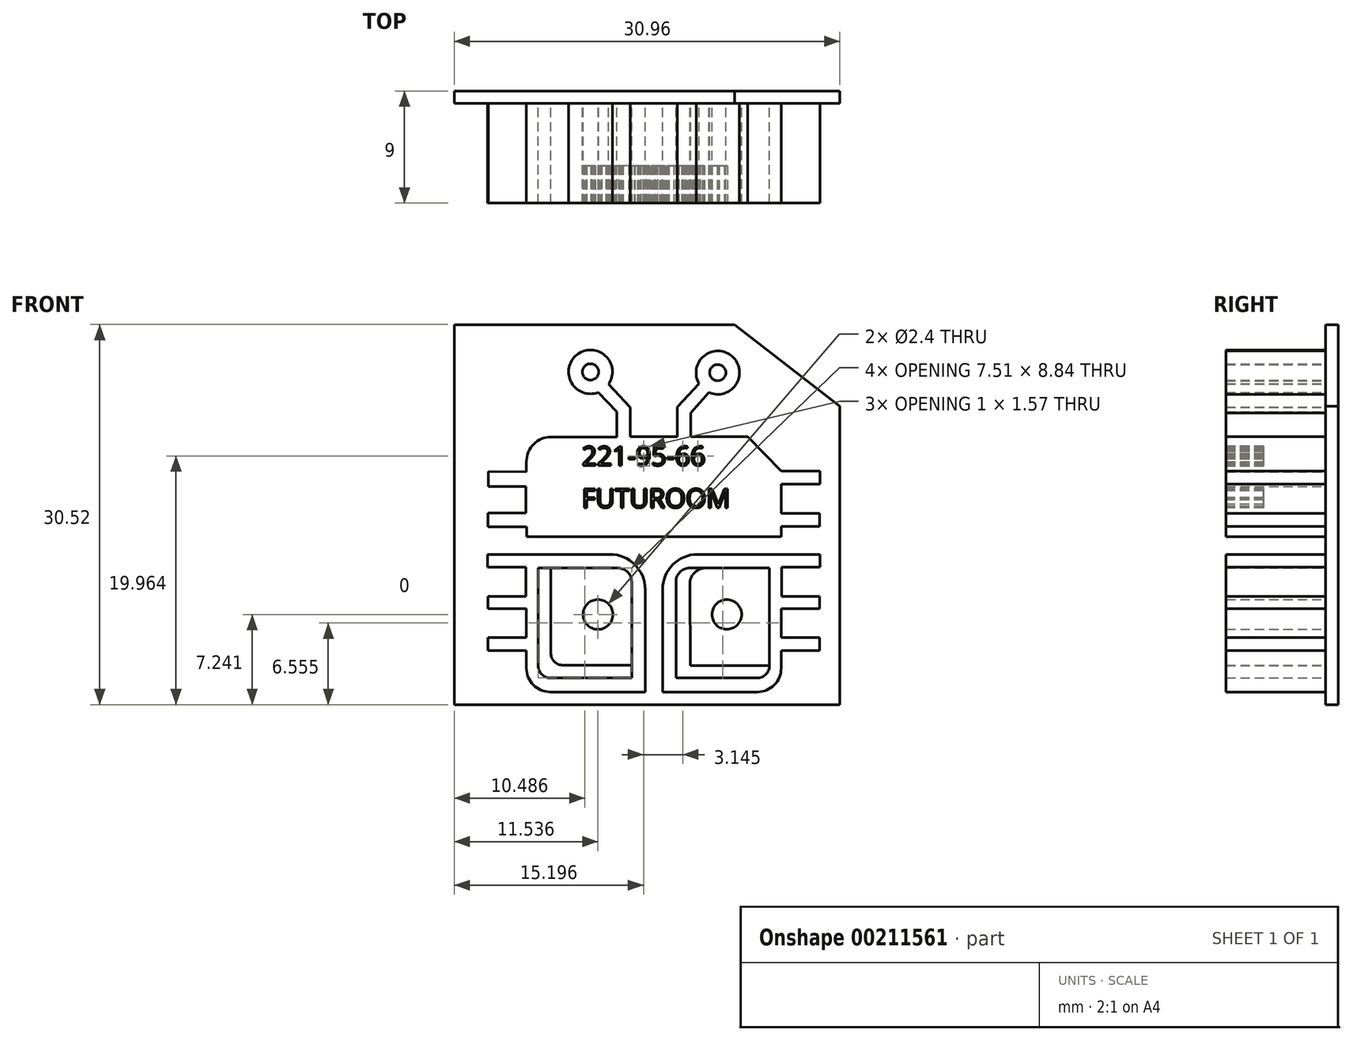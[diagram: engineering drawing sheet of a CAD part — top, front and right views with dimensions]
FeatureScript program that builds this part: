
annotation { "Feature Type Name" : "Feature", "Feature Type Description" : "" }
export const myFeature = defineFeature(function(context is Context, id is Id, definition is map)
    precondition{}
    {
        {
            var Q0;
            Q0=qCreatedBy(makeId("Front.planeOp"),FACE);
            var sketch = newSketch(context, id + "F0", { "sketchPlane" : qUnion([Q0])});
            skLineSegment(sketch, "E0", {"start": v(-14.86, -3.78) * mm, "end": v(-14.86, -5) * mm});
            skLineSegment(sketch, "E1", {"start": v(-14.86, -5) * mm, "end": v(-11.84, -5) * mm});
            skLineSegment(sketch, "E2", {"start": v(-11.84, -5) * mm, "end": v(-11.84, -7.14) * mm});
            skLineSegment(sketch, "E3", {"start": v(-11.84, -7.14) * mm, "end": v(-14.87, -7.14) * mm});
            skLineSegment(sketch, "E4", {"start": v(-14.87, -7.14) * mm, "end": v(-14.87, -8.25) * mm});
            skLineSegment(sketch, "E5", {"start": v(-14.87, -8.25) * mm, "end": v(-11.76, -8.25) * mm});
            skLineSegment(sketch, "E6", {"start": v(-11.76, -8.25) * mm, "end": v(-11.76, -9.03) * mm});
            skLineSegment(sketch, "E7", {"start": v(-11.76, -9.03) * mm, "end": v(8.67, -9.03) * mm});
            skLineSegment(sketch, "E8", {"start": v(8.67, -9.03) * mm, "end": v(8.67, -8.21) * mm});
            skLineSegment(sketch, "E9", {"start": v(8.67, -8.21) * mm, "end": v(11.76, -8.21) * mm});
            skLineSegment(sketch, "E10", {"start": v(11.76, -8.21) * mm, "end": v(11.76, -7.17) * mm});
            skLineSegment(sketch, "E11", {"start": v(11.76, -7.17) * mm, "end": v(8.68, -7.17) * mm});
            skLineSegment(sketch, "E12", {"start": v(8.68, -7.17) * mm, "end": v(8.68, -4.82) * mm});
            skLineSegment(sketch, "E13", {"start": v(8.68, -4.82) * mm, "end": v(11.8, -4.82) * mm});
            skLineSegment(sketch, "E14", {"start": v(11.8, -4.82) * mm, "end": v(11.8, -3.78) * mm});
            skLineSegment(sketch, "E15", {"start": v(11.8, -3.78) * mm, "end": v(8.68, -3.78) * mm});
            skLineSegment(sketch, "E16", {"start": v(8.68, -3.78) * mm, "end": v(5.96, -1) * mm});
            skLineSegment(sketch, "E17", {"start": v(5.96, -1) * mm, "end": v(1.42, -1) * mm});
            skLineSegment(sketch, "E18", {"start": v(1.42, -1) * mm, "end": v(1.42, 0.89) * mm});
            skLineSegment(sketch, "E19", {"start": v(1.42, 0.89) * mm, "end": v(2.86, 2.55) * mm});
            skLineSegment(sketch, "E20", {"start": v(2.08, 3.25) * mm, "end": v(0.33, 1.37) * mm});
            skLineSegment(sketch, "E21", {"start": v(0.33, 1.37) * mm, "end": v(0.33, -1) * mm});
            skLineSegment(sketch, "E22", {"start": v(0.33, -1) * mm, "end": v(-3.46, -1) * mm});
            skLineSegment(sketch, "E23", {"start": v(-3.46, -1) * mm, "end": v(-3.46, 1.34) * mm});
            skLineSegment(sketch, "E24", {"start": v(-3.46, 1.34) * mm, "end": v(-5.19, 3.2) * mm});
            skLineSegment(sketch, "E25", {"start": v(-6.02, 2.55) * mm, "end": v(-4.54, 1) * mm});
            skLineSegment(sketch, "E26", {"start": v(-4.54, 1) * mm, "end": v(-4.54, -1.02) * mm});
            skLineSegment(sketch, "E27", {"start": v(-4.54, -1.02) * mm, "end": v(-9.8, -1.02) * mm});
            skLineSegment(sketch, "E28", {"start": v(-11.8, -3.02) * mm, "end": v(-11.8, -3.82) * mm});
            skLineSegment(sketch, "E29", {"start": v(-11.8, -3.82) * mm, "end": v(-14.86, -3.78) * mm});
            skPoint(sketch, "E30.visualSharp", {"position": v(-11.8, -1.02) * mm});
            skArc(sketch, "E30.filletArc", {"start": v(-9.8, -1.02) * mm, "mid": v(-11.2, -1.6) * mm, "end": v(-11.8, -3.02) * mm});
            skArc(sketch, "E31", {"start": v(-5.19, 3.2) * mm, "mid": v(-7.73, 5.58) * mm, "end": v(-6.02, 2.55) * mm});
            skCircle(sketch, "E32", {"center": v(-6.64, 4.2) * mm, "radius": 0.65 * mm});
            skArc(sketch, "E33", {"start": v(2.86, 2.55) * mm, "mid": v(4.74, 5.44) * mm, "end": v(2.08, 3.25) * mm});
            skCircle(sketch, "E34", {"center": v(3.58, 4.14) * mm, "radius": 0.65 * mm});
            skLineSegment(sketch, "E35", {"start": v(-14.91, -10.45) * mm, "end": v(-14.91, -11.47) * mm});
            skLineSegment(sketch, "E36", {"start": v(-14.91, -11.47) * mm, "end": v(-11.84, -11.47) * mm});
            skLineSegment(sketch, "E37", {"start": v(-11.84, -11.47) * mm, "end": v(-11.84, -13.82) * mm});
            skLineSegment(sketch, "E38", {"start": v(-11.84, -13.82) * mm, "end": v(-14.89, -13.82) * mm});
            skLineSegment(sketch, "E39", {"start": v(-14.89, -13.82) * mm, "end": v(-14.89, -14.83) * mm});
            skLineSegment(sketch, "E40", {"start": v(-14.89, -14.83) * mm, "end": v(-11.79, -14.83) * mm});
            skLineSegment(sketch, "E41", {"start": v(-11.79, -14.83) * mm, "end": v(-11.79, -17.13) * mm});
            skLineSegment(sketch, "E42", {"start": v(-11.79, -17.13) * mm, "end": v(-14.87, -17.13) * mm});
            skLineSegment(sketch, "E43", {"start": v(-14.87, -17.13) * mm, "end": v(-14.87, -18.17) * mm});
            skLineSegment(sketch, "E44", {"start": v(-14.87, -18.17) * mm, "end": v(-11.79, -18.17) * mm});
            skLineSegment(sketch, "E45", {"start": v(-11.79, -18.17) * mm, "end": v(-11.79, -19.6) * mm});
            skLineSegment(sketch, "E46", {"start": v(-9.89, -21.5) * mm, "end": v(-2.26, -21.5) * mm});
            skLineSegment(sketch, "E47", {"start": v(-2.26, -21.5) * mm, "end": v(-2.26, -13.25) * mm});
            skLineSegment(sketch, "E48", {"start": v(-5.06, -10.45) * mm, "end": v(-14.91, -10.45) * mm});
            skLineSegment(sketch, "E49", {"start": v(-10.85, -11.54) * mm, "end": v(-10.85, -19.39) * mm});
            skLineSegment(sketch, "E50", {"start": v(-9.85, -20.39) * mm, "end": v(-3.34, -20.39) * mm});
            skLineSegment(sketch, "E51", {"start": v(-3.34, -20.39) * mm, "end": v(-3.34, -12.64) * mm});
            skLineSegment(sketch, "E52", {"start": v(-4.44, -11.54) * mm, "end": v(-10.85, -11.54) * mm});
            skLineSegment(sketch, "E53", {"start": v(-9.84, -11.54) * mm, "end": v(-9.84, -18.36) * mm});
            skLineSegment(sketch, "E54", {"start": v(-8.84, -19.36) * mm, "end": v(-3.34, -19.36) * mm});
            skCircle(sketch, "E55", {"center": v(-6.04, -15.28) * mm, "radius": 1.2 * mm});
            skPoint(sketch, "E56.visualSharp", {"position": v(-9.84, -19.36) * mm});
            skArc(sketch, "E56.filletArc", {"start": v(-9.84, -18.36) * mm, "mid": v(-9.54, -19.06) * mm, "end": v(-8.84, -19.36) * mm});
            skPoint(sketch, "E57.visualSharp", {"position": v(-3.34, -11.54) * mm});
            skArc(sketch, "E57.filletArc", {"start": v(-3.34, -12.64) * mm, "mid": v(-3.66, -11.87) * mm, "end": v(-4.44, -11.54) * mm});
            skPoint(sketch, "E58.visualSharp", {"position": v(-10.85, -20.39) * mm});
            skArc(sketch, "E58.filletArc", {"start": v(-10.85, -19.39) * mm, "mid": v(-10.55, -20.1) * mm, "end": v(-9.85, -20.39) * mm});
            skPoint(sketch, "E59.visualSharp", {"position": v(-11.79, -21.5) * mm});
            skArc(sketch, "E59.filletArc", {"start": v(-11.79, -19.6) * mm, "mid": v(-11.23, -20.94) * mm, "end": v(-9.89, -21.5) * mm});
            skLineSegment(sketch, "E60", {"start": v(-2.26, -21.5) * mm, "end": v(-0.86, -21.5) * mm});
            skLineSegment(sketch, "E61", {"start": v(-1.56, -21.5) * mm, "end": v(-1.56, -9.46) * mm});
            skPoint(sketch, "E62.MirrorP", {"position": v(7.73, -20.39) * mm});
            skLineSegment(sketch, "E63.MirrorCS", {"start": v(5.72, -19.36) * mm, "end": v(0.22, -19.36) * mm});
            skLineSegment(sketch, "E64.MirrorCS", {"start": v(8.72, -13.82) * mm, "end": v(11.77, -13.82) * mm});
            skLineSegment(sketch, "E65.MirrorCS", {"start": v(8.72, -11.47) * mm, "end": v(8.72, -13.82) * mm});
            skLineSegment(sketch, "E66.MirrorCS", {"start": v(1.94, -10.45) * mm, "end": v(11.8, -10.45) * mm});
            skLineSegment(sketch, "E67.MirrorCS", {"start": v(8.67, -14.83) * mm, "end": v(8.67, -17.13) * mm});
            skPoint(sketch, "E68.MirrorP", {"position": v(8.67, -21.5) * mm});
            skLineSegment(sketch, "E69.MirrorCS", {"start": v(11.77, -13.82) * mm, "end": v(11.77, -14.83) * mm});
            skArc(sketch, "E70.MirrorCS", {"start": v(8.67, -19.6) * mm, "mid": v(8.11, -20.94) * mm, "end": v(6.77, -21.5) * mm});
            skArc(sketch, "E71.MirrorCS", {"start": v(0.22, -12.64) * mm, "mid": v(0.55, -11.87) * mm, "end": v(1.32, -11.54) * mm});
            skLineSegment(sketch, "E72.MirrorCS", {"start": v(6.73, -20.39) * mm, "end": v(0.22, -20.39) * mm});
            skLineSegment(sketch, "E73.MirrorCS", {"start": v(11.76, -17.13) * mm, "end": v(11.76, -18.17) * mm});
            skLineSegment(sketch, "E74.MirrorCS", {"start": v(11.8, -10.45) * mm, "end": v(11.8, -11.47) * mm});
            skLineSegment(sketch, "E75.MirrorCS", {"start": v(0.22, -20.39) * mm, "end": v(0.22, -12.64) * mm});
            skLineSegment(sketch, "E76.MirrorCS", {"start": v(11.76, -18.17) * mm, "end": v(8.67, -18.17) * mm});
            skPoint(sketch, "E77.MirrorP", {"position": v(0.22, -11.54) * mm});
            skPoint(sketch, "E78.MirrorP", {"position": v(6.72, -19.36) * mm});
            skLineSegment(sketch, "E79.MirrorCS", {"start": v(8.67, -17.13) * mm, "end": v(11.76, -17.13) * mm});
            skLineSegment(sketch, "E80.MirrorCS", {"start": v(7.73, -11.54) * mm, "end": v(7.73, -19.39) * mm});
            skLineSegment(sketch, "E81.MirrorCS", {"start": v(-0.86, -21.5) * mm, "end": v(-0.86, -13.25) * mm});
            skLineSegment(sketch, "E82.MirrorCS", {"start": v(2.63, -11.54) * mm, "end": v(7.73, -11.54) * mm});
            skArc(sketch, "E83.MirrorCS", {"start": v(7.73, -19.39) * mm, "mid": v(7.44, -20.1) * mm, "end": v(6.73, -20.39) * mm});
            skLineSegment(sketch, "E84.MirrorCS", {"start": v(11.77, -14.83) * mm, "end": v(8.67, -14.83) * mm});
            skLineSegment(sketch, "E85.MirrorCS", {"start": v(11.8, -11.47) * mm, "end": v(8.72, -11.47) * mm});
            skLineSegment(sketch, "E86.MirrorCS", {"start": v(8.67, -18.17) * mm, "end": v(8.67, -19.6) * mm});
            skLineSegment(sketch, "E87", {"start": v(7.73, -19.39) * mm, "end": v(1.38, -19.39) * mm});
            skLineSegment(sketch, "E88", {"start": v(1.38, -19.39) * mm, "end": v(1.33, -12.85) * mm});
            skPoint(sketch, "E89.visualSharp", {"position": v(1.32, -11.54) * mm});
            skArc(sketch, "E89.filletArc", {"start": v(2.63, -11.54) * mm, "mid": v(1.71, -11.93) * mm, "end": v(1.33, -12.85) * mm});
            skCircle(sketch, "E90", {"center": v(4.3, -15.28) * mm, "radius": 1.2 * mm});
            skPoint(sketch, "E91.visualSharp", {"position": v(-10.78, -2.08) * mm});
            skLineSegment(sketch, "E92", {"start": v(-0.86, -21.5) * mm, "end": v(6.77, -21.5) * mm});
            skLineSegment(sketch, "E93", {"start": v(1.32, -11.54) * mm, "end": v(2.95, -11.54) * mm});
            skPoint(sketch, "E94.visualSharp", {"position": v(-2.26, -10.45) * mm});
            skArc(sketch, "E94.filletArc", {"start": v(-2.26, -13.25) * mm, "mid": v(-3.08, -11.27) * mm, "end": v(-5.06, -10.45) * mm});
            skPoint(sketch, "E95.visualSharp", {"position": v(-0.86, -10.45) * mm});
            skArc(sketch, "E95.filletArc", {"start": v(1.94, -10.45) * mm, "mid": v(-0.04, -11.27) * mm, "end": v(-0.86, -13.25) * mm});
            skSolve(sketch);
        }
        {
            var Q0;
            Q0=makeQuery(id+"F0.imprint","IMPRINT",FACE,{"disambiguationData":[TD([[makeQuery(id+"F0.imprint","IMPRINT",EDGE,{"derivedFrom":sQuery(id+"F0.wireOp",EDGE,"E35")}),1.0]])]});
            var Q1;
            Q1=makeQuery(id+"F0.imprint","IMPRINT",FACE,{"disambiguationData":[TD([[makeQuery(id+"F0.imprint","IMPRINT",EDGE,{"derivedFrom":sQuery(id+"F0.wireOp",EDGE,"E0")}),1.0]])]});
            var Q2;
            {var subQ1=sQuery(id+"F0.wireOp",EDGE,"E53");Q2=makeQuery(id+"F0.imprint","IMPRINT",FACE,{"disambiguationData":[TD([[makeQuery(id+"F0.imprint","IMPRINT",EDGE,{"derivedFrom":subQ1}),1.0]])]});}
            var Q3;
            Q3=makeQuery(id+"F0.imprint","IMPRINT",FACE,{"disambiguationData":[TD([[makeQuery(id+"F0.imprint","IMPRINT",EDGE,{"derivedFrom":sQuery(id+"F0.wireOp",EDGE,"E80.MirrorCS")}),-1.0]])]});
            extrude(context, id + "F1", {"entities" : qUnion([Q0, Q1, Q2, Q3]), "depth" : 8 * mm});
        }
        {
            var Q0;
            Q0 = qSketchRegion(id + "F0", true);
            extrude(context, id + "F2", {"entities" : qUnion([Q0]), "depth" : 8 * mm});
        }
        {
            var Q0;
            Q0=qCreatedBy(makeId("Front.planeOp"),FACE);
            var sketch = newSketch(context, id + "F3", { "sketchPlane" : qUnion([Q0])});
            skLineSegment(sketch, "E96", {"start": v(-17.58, 7.3) * mm, "end": v(-17.58, -22.52) * mm});
            skLineSegment(sketch, "E97", {"start": v(-17.58, -22.52) * mm, "end": v(13.38, -22.52) * mm});
            skLineSegment(sketch, "E98", {"start": v(13.38, -22.52) * mm, "end": v(13.38, 1.46) * mm});
            skLineSegment(sketch, "E99", {"start": v(13.38, 1.46) * mm, "end": v(4.92, 8) * mm});
            skLineSegment(sketch, "E100", {"start": v(4.92, 8) * mm, "end": v(-17.58, 8) * mm});
            skLineSegment(sketch, "E101", {"start": v(-17.58, 8) * mm, "end": v(-17.58, 7.3) * mm});
            skSolve(sketch);
        }
        {
            var Q0;
            Q0 = qSketchRegion(id + "F3", true);
            extrude(context, id + "F4", {"entities" : qUnion([Q0]), "oppositeDirection" : true, "depth" : 1 * mm});
        }
        {
            var Q0;
            Q0=makeQuery(id+"F2.opExtrude","CAP_FACE",FACE,{"disambiguationData":[OSD([sQuery(id+"F0.wireOp",EDGE,"E0"),sQuery(id+"F0.wireOp",EDGE,"E1"),sQuery(id+"F0.wireOp",EDGE,"E2"),sQuery(id+"F0.wireOp",EDGE,"E3"),sQuery(id+"F0.wireOp",EDGE,"E4"),sQuery(id+"F0.wireOp",EDGE,"E5"),sQuery(id+"F0.wireOp",EDGE,"E6"),sQuery(id+"F0.wireOp",EDGE,"E7"),sQuery(id+"F0.wireOp",EDGE,"E8"),sQuery(id+"F0.wireOp",EDGE,"E9"),sQuery(id+"F0.wireOp",EDGE,"E10"),sQuery(id+"F0.wireOp",EDGE,"E11"),sQuery(id+"F0.wireOp",EDGE,"E12"),sQuery(id+"F0.wireOp",EDGE,"E13"),sQuery(id+"F0.wireOp",EDGE,"E14"),sQuery(id+"F0.wireOp",EDGE,"E15"),sQuery(id+"F0.wireOp",EDGE,"E16"),sQuery(id+"F0.wireOp",EDGE,"E17"),sQuery(id+"F0.wireOp",EDGE,"E18"),sQuery(id+"F0.wireOp",EDGE,"E19"),sQuery(id+"F0.wireOp",EDGE,"E20"),sQuery(id+"F0.wireOp",EDGE,"E21"),sQuery(id+"F0.wireOp",EDGE,"E22"),sQuery(id+"F0.wireOp",EDGE,"E23"),sQuery(id+"F0.wireOp",EDGE,"E24"),sQuery(id+"F0.wireOp",EDGE,"E25"),sQuery(id+"F0.wireOp",EDGE,"E26"),sQuery(id+"F0.wireOp",EDGE,"E27"),sQuery(id+"F0.wireOp",EDGE,"E28"),sQuery(id+"F0.wireOp",EDGE,"E29"),sQuery(id+"F0.wireOp",EDGE,"E30.filletArc"),sQuery(id+"F0.wireOp",EDGE,"E31"),sQuery(id+"F0.wireOp",EDGE,"E32"),sQuery(id+"F0.wireOp",EDGE,"E33"),sQuery(id+"F0.wireOp",EDGE,"E34"),sQuery(id+"F0.wireOp",EDGE,"xEMdINrW-eBVi-GkxS-4sBf-KnaFbcdrDIeM"),sQuery(id+"F0.wireOp",EDGE,"bnCL2eH6-rMTv-iHCu-9fqk-YgjS3GXMpQWJ"),sQuery(id+"F0.wireOp",EDGE,"BFUH8g3K-GC5Y-QA6M-1HIY-HL1wT416Nki4"),sQuery(id+"F0.wireOp",EDGE,"c6946ad9-822f-4685-8c8e-a4172cfd5702"),sQuery(id+"F0.wireOp",EDGE,"h1fRMnBA-cXQm-W97X-tv0y-zpCmJUFAqdWb"),sQuery(id+"F0.wireOp",EDGE,"E91.filletArc")])],"isStart":false});
            var sketch = newSketch(context, id + "F5", { "sketchPlane" : qUnion([Q0])});
            skText(sketch, "E102", { "text": "221-95-66", "fontName": "OpenSans-Regular.ttf"});
            skText(sketch, "E103", { "text": "FUTUROOM", "fontName": "OpenSans-Regular.ttf"});
            const initialGuessF5  = {"E102": [-0.00735, -0.00332, 1, 0, 0.00154], "E103": [-0.00733, -0.00671, 1, 0, 0.00153]};
            skSetInitialGuess(sketch, initialGuessF5);
            skSolve(sketch);
        }
        {
            var Q0;
            Q0 = qSketchRegion(id + "F5", true);
            extrude(context, id + "F6", {"entities" : qUnion([Q0]), "operationType" : NewBodyOperationType.REMOVE, "oppositeDirection" : true, "depth" : 3 * mm});
        }
        {
            var Q0;
            Q0=makeQuery(id+"F1.opExtrude","SWEPT_BODY",BODY,{"disambiguationData":[OSD([sQuery(id+"F0.wireOp",EDGE,"E35"),sQuery(id+"F0.wireOp",EDGE,"E36"),sQuery(id+"F0.wireOp",EDGE,"E37"),sQuery(id+"F0.wireOp",EDGE,"E38"),sQuery(id+"F0.wireOp",EDGE,"E39"),sQuery(id+"F0.wireOp",EDGE,"E40"),sQuery(id+"F0.wireOp",EDGE,"E41"),sQuery(id+"F0.wireOp",EDGE,"E42"),sQuery(id+"F0.wireOp",EDGE,"E43"),sQuery(id+"F0.wireOp",EDGE,"E44"),sQuery(id+"F0.wireOp",EDGE,"E45"),sQuery(id+"F0.wireOp",EDGE,"E46"),sQuery(id+"F0.wireOp",EDGE,"E47"),sQuery(id+"F0.wireOp",EDGE,"E48"),sQuery(id+"F0.wireOp",EDGE,"E49"),sQuery(id+"F0.wireOp",EDGE,"E50"),sQuery(id+"F0.wireOp",EDGE,"E51"),sQuery(id+"F0.wireOp",EDGE,"E52"),sQuery(id+"F0.wireOp",EDGE,"E53"),sQuery(id+"F0.wireOp",EDGE,"E54"),sQuery(id+"F0.wireOp",EDGE,"E55"),sQuery(id+"F0.wireOp",EDGE,"E56.filletArc"),sQuery(id+"F0.wireOp",EDGE,"E58.filletArc"),sQuery(id+"F0.wireOp",EDGE,"E59.filletArc"),sQuery(id+"F0.wireOp",EDGE,"E94.filletArc")])]});
            transform(context, id + "F7", {"entities" : qUnion([Q0]), "transformType" : TransformType.TRANSLATION_3D, "dx" : 0 * mm, "dy" : 0 * mm, "dz" : 0 * mm, "makeCopy" : true});
        }
    });
